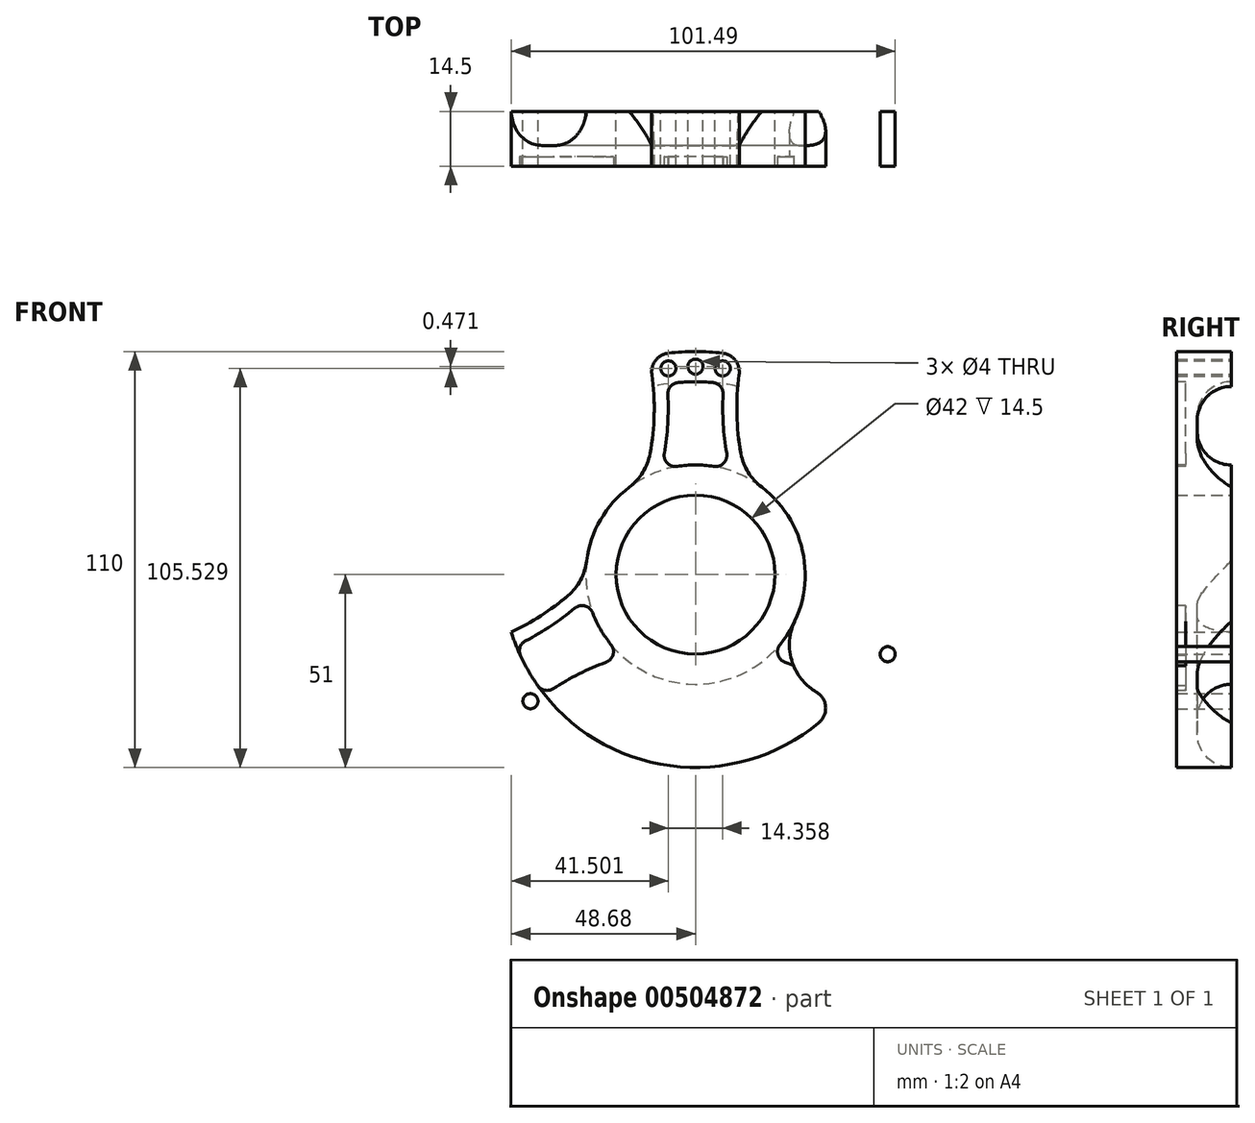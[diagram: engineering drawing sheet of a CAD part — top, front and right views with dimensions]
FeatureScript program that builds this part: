
annotation { "Feature Type Name" : "Feature", "Feature Type Description" : "" }
export const myFeature = defineFeature(function(context is Context, id is Id, definition is map)
    precondition{}
    {
        {
            var Q0;
            Q0=qCreatedBy(makeId("Front.planeOp"),FACE);
            var sketch = newSketch(context, id + "F0", { "sketchPlane" : qUnion([Q0])});
            skCircle(sketch, "E0", {"center": v(0, 0) * mm, "radius": 59 * mm});
            skCircle(sketch, "E1", {"center": v(0, 0) * mm, "radius": 51 * mm});
            skCircle(sketch, "E2", {"center": v(0, 55) * mm, "radius": 2 * mm});
            skCircle(sketch, "E3", {"center": v(7.18, 54.53) * mm, "radius": 2 * mm});
            skLineSegment(sketch, "E4", {"start": v(0, 55) * mm, "end": v(0, 0) * mm});
            skLineSegment(sketch, "E5", {"start": v(7.18, 54.53) * mm, "end": v(0, 0) * mm});
            skCircle(sketch, "E6.MirrorC", {"center": v(-7.18, 54.53) * mm, "radius": 2 * mm});
            skCircle(sketch, "E7.1.0", {"center": v(-43.63, -33.48) * mm, "radius": 2 * mm});
            skCircle(sketch, "E7.1.1", {"center": v(-47.63, -27.5) * mm, "radius": 2 * mm});
            skCircle(sketch, "E7.1.2", {"center": v(-50.81, -21.05) * mm, "radius": 2 * mm});
            skCircle(sketch, "E7.2.0", {"center": v(50.81, -21.05) * mm, "radius": 2 * mm});
            skCircle(sketch, "E7.2.1", {"center": v(47.63, -27.5) * mm, "radius": 2 * mm});
            skCircle(sketch, "E7.2.2", {"center": v(43.63, -33.48) * mm, "radius": 2 * mm});
            skCircle(sketch, "E8", {"center": v(0, 0) * mm, "radius": 21 * mm});
            skArc(sketch, "E9", {"start": v(43.78, -39.56) * mm, "mid": v(0, -22.7) * mm, "end": v(-43.78, -39.56) * mm});
            skLineSegment(sketch, "E10", {"start": v(0, -88) * mm, "end": v(43.78, -39.56) * mm});
            skLineSegment(sketch, "E11", {"start": v(0, -88) * mm, "end": v(-43.78, -39.56) * mm});
            skArc(sketch, "E12.1.0", {"start": v(12.37, 57.69) * mm, "mid": v(19.67, 11.35) * mm, "end": v(56.14, -18.13) * mm});
            skArc(sketch, "E12.2.0", {"start": v(-56.14, -18.13) * mm, "mid": v(-19.67, 11.35) * mm, "end": v(-12.37, 57.69) * mm});
            skCircle(sketch, "E13", {"center": v(0, 0) * mm, "radius": 29 * mm});
            skSolve(sketch);
        }
        {
            var Q0;
            Q0=qCreatedBy(makeId("Right.planeOp"),FACE);
            var sketch = newSketch(context, id + "F1", { "sketchPlane" : qUnion([Q0])});
            skSolve(sketch);
        }
        {
            var Q0;
            Q0=qSketchRegion(id+"F1",true);
            var Q1;
            Q1=makeQuery(id+"F0.imprint","IMPRINT",FACE,{"disambiguationData":[TD([[makeQuery(id+"F0.imprint","IMPRINT",EDGE,{"derivedFrom":sQuery(id+"F0.wireOp",EDGE,"E2")}),-1.0]])]});
            var Q2;
            {var subQ0=sQuery(id+"F0.wireOp",EDGE,"E4");var subQ1=sQuery(id+"F0.wireOp",EDGE,"E1");var subQ2=makeQuery(id+"F0.imprint","INTERSECT",VERTEX,{"derivedFrom":[subQ1,subQ0]});Q2=makeQuery(id+"F0.imprint","IMPRINT",FACE,{"disambiguationData":[TD([[makeQuery(id+"F0.imprint","IMPRINT",EDGE,{"disambiguationData":[TD([[subQ2,-1.0]])],"derivedFrom":subQ1}),1.0]])]});}
            var Q3;
            {var subQ0=sQuery(id+"F0.wireOp",EDGE,"E5");var subQ1=sQuery(id+"F0.wireOp",EDGE,"E1");var subQ2=makeQuery(id+"F0.imprint","INTERSECT",VERTEX,{"derivedFrom":[subQ1,subQ0]});Q3=makeQuery(id+"F0.imprint","IMPRINT",FACE,{"disambiguationData":[TD([[makeQuery(id+"F0.imprint","IMPRINT",EDGE,{"disambiguationData":[TD([[subQ2,-1.0]])],"derivedFrom":subQ1}),1.0]])]});}
            var Q4;
            {var subQ0=sQuery(id+"F0.wireOp",EDGE,"E5");var subQ1=sQuery(id+"F0.wireOp",EDGE,"E1");var subQ2=makeQuery(id+"F0.imprint","INTERSECT",VERTEX,{"derivedFrom":[subQ1,subQ0]});Q4=makeQuery(id+"F0.imprint","IMPRINT",FACE,{"disambiguationData":[TD([[makeQuery(id+"F0.imprint","IMPRINT",EDGE,{"disambiguationData":[TD([[subQ2,1.0]])],"derivedFrom":subQ1}),1.0]])]});}
            var Q5;
            {var subQ0=sQuery(id+"F0.wireOp",EDGE,"E13");var subQ5=sQuery(id+"F0.wireOp",EDGE,"E4");var subQ12=makeQuery(id+"F0.imprint","INTERSECT",VERTEX,{"derivedFrom":[subQ5,subQ0]});Q5=makeQuery(id+"F0.imprint","IMPRINT",FACE,{"disambiguationData":[TD([[makeQuery(id+"F0.imprint","IMPRINT",EDGE,{"disambiguationData":[TD([[subQ12,-1.0]])],"derivedFrom":subQ5}),-1.0]])]});}
            var Q6;
            {var subQ0=sQuery(id+"F0.wireOp",EDGE,"E13");var subQ1=sQuery(id+"F0.wireOp",EDGE,"E4");var subQ2=makeQuery(id+"F0.imprint","INTERSECT",VERTEX,{"derivedFrom":[subQ1,subQ0]});Q6=makeQuery(id+"F0.imprint","IMPRINT",FACE,{"disambiguationData":[TD([[makeQuery(id+"F0.imprint","IMPRINT",EDGE,{"disambiguationData":[TD([[subQ2,-1.0]])],"derivedFrom":subQ1}),1.0]])]});}
            var Q7;
            {var subQ0=sQuery(id+"F0.wireOp",EDGE,"E13");var subQ1=sQuery(id+"F0.wireOp",EDGE,"E12.2.0");var subQ2=makeQuery(id+"F0.imprint","INTERSECT",VERTEX,{"disambiguationData":[OD(0.0)],"derivedFrom":[subQ1,subQ0]});Q7=makeQuery(id+"F0.imprint","IMPRINT",FACE,{"disambiguationData":[TD([[makeQuery(id+"F0.imprint","IMPRINT",EDGE,{"disambiguationData":[TD([[subQ2,-1.0]])],"derivedFrom":subQ1}),1.0]])]});}
            var Q8;
            {var subQ0=sQuery(id+"F0.wireOp",EDGE,"E13");var subQ1=sQuery(id+"F0.wireOp",EDGE,"E12.1.0");var subQ2=makeQuery(id+"F0.imprint","INTERSECT",VERTEX,{"disambiguationData":[OD(0.0)],"derivedFrom":[subQ1,subQ0]});Q8=makeQuery(id+"F0.imprint","IMPRINT",FACE,{"disambiguationData":[TD([[makeQuery(id+"F0.imprint","IMPRINT",EDGE,{"disambiguationData":[TD([[subQ2,-1.0]])],"derivedFrom":subQ1}),1.0]])]});}
            var Q9;
            {var subQ0=sQuery(id+"F0.wireOp",EDGE,"E13");var subQ1=sQuery(id+"F0.wireOp",EDGE,"E9");var subQ2=makeQuery(id+"F0.imprint","INTERSECT",VERTEX,{"disambiguationData":[OD(0.0)],"derivedFrom":[subQ1,subQ0]});Q9=makeQuery(id+"F0.imprint","IMPRINT",FACE,{"disambiguationData":[TD([[makeQuery(id+"F0.imprint","IMPRINT",EDGE,{"disambiguationData":[TD([[subQ2,-1.0]])],"derivedFrom":subQ1}),1.0]])]});}
            var Q10;
            {var subQ0=sQuery(id+"F0.wireOp",EDGE,"E12.2.0");var subQ1=sQuery(id+"F0.wireOp",EDGE,"E1");var subQ2=makeQuery(id+"F0.imprint","INTERSECT",VERTEX,{"disambiguationData":[OD(1.0)],"derivedFrom":[subQ1,subQ0]});Q10=makeQuery(id+"F0.imprint","IMPRINT",FACE,{"disambiguationData":[TD([[makeQuery(id+"F0.imprint","IMPRINT",EDGE,{"disambiguationData":[TD([[subQ2,-1.0]])],"derivedFrom":subQ1}),1.0]])]});}
            var Q11;
            {var subQ0=sQuery(id+"F0.wireOp",EDGE,"E9");var subQ1=sQuery(id+"F0.wireOp",EDGE,"E1");var subQ2=makeQuery(id+"F0.imprint","INTERSECT",VERTEX,{"disambiguationData":[OD(1.0)],"derivedFrom":[subQ1,subQ0]});Q11=makeQuery(id+"F0.imprint","IMPRINT",FACE,{"disambiguationData":[TD([[makeQuery(id+"F0.imprint","IMPRINT",EDGE,{"disambiguationData":[TD([[subQ2,-1.0]])],"derivedFrom":subQ1}),1.0]])]});}
            var Q12;
            Q12=makeQuery(id+"F0.imprint","IMPRINT",FACE,{"disambiguationData":[TD([[makeQuery(id+"F0.imprint","IMPRINT",EDGE,{"derivedFrom":sQuery(id+"F0.wireOp",EDGE,"E7.2.0")}),1.0]])]});
            var Q13;
            Q13=makeQuery(id+"F0.imprint","IMPRINT",FACE,{"disambiguationData":[TD([[makeQuery(id+"F0.imprint","IMPRINT",EDGE,{"derivedFrom":sQuery(id+"F0.wireOp",EDGE,"E7.1.0")}),1.0]])]});
            extrude(context, id + "F2", {"entities" : qUnion([Q0, Q1, Q2, Q3, Q4, Q5, Q6, Q7, Q8, Q9, Q10, Q11, Q12, Q13]), "depth" : 14.5 * mm});
        }
        {
            var Q0;
            Q0=qCreatedBy(makeId("Right.planeOp"),FACE);
            var sketch = newSketch(context, id + "F3", { "sketchPlane" : qUnion([Q0])});
            skLineSegment(sketch, "E14.bottom", {"start": v(0, 51) * mm, "end": v(0, 51) * mm});
            skLineSegment(sketch, "E14.top", {"start": v(0, 0) * mm, "end": v(0, 0) * mm});
            skLineSegment(sketch, "E14.left", {"start": v(0, 51) * mm, "end": v(0, 29) * mm});
            skLineSegment(sketch, "E14.right", {"start": v(-9, 42) * mm, "end": v(-9, 38) * mm});
            skArc(sketch, "E15.filletArc", {"start": v(0, 51) * mm, "mid": v(-6.36, 48.36) * mm, "end": v(-9, 42) * mm});
            skArc(sketch, "E16", {"start": v(-9, 38) * mm, "mid": v(-6.36, 31.64) * mm, "end": v(0, 29) * mm});
            skSolve(sketch);
        }
        {
            var Q0;
            Q0=qSketchRegion(id+"F3",true);
            var Q1;
            Q1=sQuery(id+"F0.wireOp",EDGE,"E0");
            revolve(context, id + "F4", {"operationType" : NewBodyOperationType.REMOVE, "entities" : qUnion([Q0]), "axis" : qUnion([Q1]), "revolveType" : RevolveType.FULL});
        }
        {
            var Q0;
            {var subQ0=sQuery(id+"F0.wireOp",EDGE,"E13");var subQ1=sQuery(id+"F0.wireOp",EDGE,"E12.1.0");Q0=makeQuery(id+"F2.opExtrude","SWEPT_EDGE",EDGE,{"disambiguationData":[OSD([subQ1,subQ0]),TDD([makeQuery(id+"F0.imprint","INTERSECT",VERTEX,{"disambiguationData":[OD(0.0)],"derivedFrom":[subQ1,subQ0]})])]});}
            var Q1;
            {var subQ0=sQuery(id+"F0.wireOp",EDGE,"E13");var subQ1=sQuery(id+"F0.wireOp",EDGE,"E12.1.0");Q1=makeQuery(id+"F2.opExtrude","SWEPT_EDGE",EDGE,{"disambiguationData":[OSD([subQ1,subQ0]),TDD([makeQuery(id+"F0.imprint","INTERSECT",VERTEX,{"disambiguationData":[OD(1.0)],"derivedFrom":[subQ1,subQ0]})])]});}
            var Q2;
            {var subQ0=sQuery(id+"F0.wireOp",EDGE,"E13");var subQ1=sQuery(id+"F0.wireOp",EDGE,"E12.2.0");Q2=makeQuery(id+"F2.opExtrude","SWEPT_EDGE",EDGE,{"disambiguationData":[OSD([subQ1,subQ0]),TDD([makeQuery(id+"F0.imprint","INTERSECT",VERTEX,{"disambiguationData":[OD(0.0)],"derivedFrom":[subQ1,subQ0]})])]});}
            var Q3;
            {var subQ0=sQuery(id+"F0.wireOp",EDGE,"E13");var subQ1=sQuery(id+"F0.wireOp",EDGE,"E12.2.0");Q3=makeQuery(id+"F2.opExtrude","SWEPT_EDGE",EDGE,{"disambiguationData":[OSD([subQ1,subQ0]),TDD([makeQuery(id+"F0.imprint","INTERSECT",VERTEX,{"disambiguationData":[OD(1.0)],"derivedFrom":[subQ1,subQ0]})])]});}
            var Q4;
            {var subQ0=sQuery(id+"F0.wireOp",EDGE,"E13");var subQ1=sQuery(id+"F0.wireOp",EDGE,"E9");Q4=makeQuery(id+"F2.opExtrude","SWEPT_EDGE",EDGE,{"disambiguationData":[OSD([subQ1,subQ0]),TDD([makeQuery(id+"F0.imprint","INTERSECT",VERTEX,{"disambiguationData":[OD(1.0)],"derivedFrom":[subQ1,subQ0]})])]});}
            var Q5;
            {var subQ0=sQuery(id+"F0.wireOp",EDGE,"E13");var subQ1=sQuery(id+"F0.wireOp",EDGE,"E9");Q5=makeQuery(id+"F2.opExtrude","SWEPT_EDGE",EDGE,{"disambiguationData":[OSD([subQ1,subQ0]),TDD([makeQuery(id+"F0.imprint","INTERSECT",VERTEX,{"disambiguationData":[OD(0.0)],"derivedFrom":[subQ1,subQ0]})])]});}
            fillet(context, id + "F5", {"entities" : qUnion([Q0, Q1, Q2, Q3, Q4, Q5]), "radius" : 14.5 * mm, "tangentPropagation" : true, "allowEdgeOverflow" : false});
        }
        {
            var Q0;
            {var subQ0=sQuery(id+"F0.wireOp",EDGE,"E12.1.0");var subQ1=sQuery(id+"F0.wireOp",EDGE,"E0");Q0=makeQuery(id+"F2.opExtrude","SWEPT_EDGE",EDGE,{"disambiguationData":[OSD([subQ1,subQ0]),TDD([makeQuery(id+"F0.imprint","INTERSECT",VERTEX,{"disambiguationData":[OD(0.0)],"derivedFrom":[subQ1,subQ0]})])]});}
            var Q1;
            {var subQ0=sQuery(id+"F0.wireOp",EDGE,"E12.2.0");var subQ1=sQuery(id+"F0.wireOp",EDGE,"E0");Q1=makeQuery(id+"F2.opExtrude","SWEPT_EDGE",EDGE,{"disambiguationData":[OSD([subQ1,subQ0]),TDD([makeQuery(id+"F0.imprint","INTERSECT",VERTEX,{"disambiguationData":[OD(1.0)],"derivedFrom":[subQ1,subQ0]})])]});}
            var Q2;
            {var subQ0=sQuery(id+"F0.wireOp",EDGE,"E12.2.0");var subQ1=sQuery(id+"F0.wireOp",EDGE,"E0");Q2=makeQuery(id+"F2.opExtrude","SWEPT_EDGE",EDGE,{"disambiguationData":[OSD([subQ1,subQ0]),TDD([makeQuery(id+"F0.imprint","INTERSECT",VERTEX,{"disambiguationData":[OD(0.0)],"derivedFrom":[subQ1,subQ0]})])]});}
            var Q3;
            {var subQ0=sQuery(id+"F0.wireOp",EDGE,"E12.1.0");var subQ1=sQuery(id+"F0.wireOp",EDGE,"E0");Q3=makeQuery(id+"F2.opExtrude","SWEPT_EDGE",EDGE,{"disambiguationData":[OSD([subQ1,subQ0]),TDD([makeQuery(id+"F0.imprint","INTERSECT",VERTEX,{"disambiguationData":[OD(1.0)],"derivedFrom":[subQ1,subQ0]})])]});}
            var Q4;
            Q4=makeQuery(id+"F2.opExtrude","SWEPT_EDGE",EDGE,{"disambiguationData":[OSD([sQuery(id+"F0.wireOp",EDGE,"E0"),sQuery(id+"F0.wireOp",EDGE,"E9"),sQuery(id+"F0.wireOp",EDGE,"E11")])]});
            var Q5;
            Q5=makeQuery(id+"F2.opExtrude","SWEPT_EDGE",EDGE,{"disambiguationData":[OSD([sQuery(id+"F0.wireOp",EDGE,"E0"),sQuery(id+"F0.wireOp",EDGE,"E9"),sQuery(id+"F0.wireOp",EDGE,"E10")])]});
            fillet(context, id + "F6", {"entities" : qUnion([Q0, Q1, Q2, Q3, Q4, Q5]), "radius" : 5 * mm, "tangentPropagation" : true, "allowEdgeOverflow" : false});
        }
        {
            var Q0;
            Q0=makeQuery(id+"F2.opExtrude","CAP_FACE",FACE,{"disambiguationData":[OSD([sQuery(id+"F0.wireOp",EDGE,"E0"),sQuery(id+"F0.wireOp",EDGE,"E2"),sQuery(id+"F0.wireOp",EDGE,"E3"),sQuery(id+"F0.wireOp",EDGE,"E6.MirrorC"),sQuery(id+"F0.wireOp",EDGE,"E7.1.0"),sQuery(id+"F0.wireOp",EDGE,"E7.1.1"),sQuery(id+"F0.wireOp",EDGE,"E7.1.2"),sQuery(id+"F0.wireOp",EDGE,"E7.2.0"),sQuery(id+"F0.wireOp",EDGE,"E7.2.1"),sQuery(id+"F0.wireOp",EDGE,"E7.2.2"),sQuery(id+"F0.wireOp",EDGE,"E8"),sQuery(id+"F0.wireOp",EDGE,"E9"),sQuery(id+"F0.wireOp",EDGE,"E12.1.0"),sQuery(id+"F0.wireOp",EDGE,"E12.2.0"),sQuery(id+"F0.wireOp",EDGE,"E13")])],"isStart":false});
            var sketch = newSketch(context, id + "F7", { "sketchPlane" : qUnion([Q0])});
            skArc(sketch, "E17", {"start": v(22.37, -18.45) * mm, "mid": v(25.11, -14.5) * mm, "end": v(27.17, -10.15) * mm});
            skArc(sketch, "E18", {"start": v(-46.28, -21.43) * mm, "mid": v(-44.17, -25.5) * mm, "end": v(-41.7, -29.36) * mm});
            skArc(sketch, "E19", {"start": v(-44.92, -17.5) * mm, "mid": v(-38.17, -13.56) * mm, "end": v(-31.9, -8.9) * mm});
            skArc(sketch, "E20", {"start": v(7.3, 47.65) * mm, "mid": v(7.34, 39.84) * mm, "end": v(8.25, 32.08) * mm});
            skArc(sketch, "E21.trimOffspring", {"start": v(-8.25, 32.08) * mm, "mid": v(-7.34, 39.84) * mm, "end": v(-7.3, 47.65) * mm});
            skArc(sketch, "E22.trimOffspring", {"start": v(31.9, -8.9) * mm, "mid": v(38.17, -13.56) * mm, "end": v(44.92, -17.5) * mm});
            skArc(sketch, "E23", {"start": v(37.61, -30.15) * mm, "mid": v(30.83, -26.27) * mm, "end": v(23.66, -23.18) * mm});
            skArc(sketch, "E24.trimOffspring", {"start": v(-23.66, -23.18) * mm, "mid": v(-30.83, -26.27) * mm, "end": v(-37.61, -30.15) * mm});
            skArc(sketch, "E25.trimOffspring", {"start": v(4.58, 50.8) * mm, "mid": v(0, 51) * mm, "end": v(-4.58, 50.8) * mm});
            skArc(sketch, "E26.trimOffspring", {"start": v(41.7, -29.36) * mm, "mid": v(44.17, -25.5) * mm, "end": v(46.28, -21.43) * mm});
            skArc(sketch, "E27.trimOffspring", {"start": v(4.8, 28.6) * mm, "mid": v(0, 29) * mm, "end": v(-4.8, 28.6) * mm});
            skArc(sketch, "E28.trimOffspring", {"start": v(-27.17, -10.15) * mm, "mid": v(-25.11, -14.5) * mm, "end": v(-22.37, -18.45) * mm});
            skPoint(sketch, "E29.visualSharp", {"position": v(-9.21, 27.5) * mm});
            skArc(sketch, "E29.filletArc", {"start": v(-8.25, 32.08) * mm, "mid": v(-7.42, 29.45) * mm, "end": v(-4.8, 28.6) * mm});
            skPoint(sketch, "E30.visualSharp", {"position": v(9.21, 27.5) * mm});
            skArc(sketch, "E30.filletArc", {"start": v(4.8, 28.6) * mm, "mid": v(7.42, 29.45) * mm, "end": v(8.25, 32.08) * mm});
            skPoint(sketch, "E31.visualSharp", {"position": v(-7.51, 50.44) * mm});
            skArc(sketch, "E31.filletArc", {"start": v(-4.58, 50.8) * mm, "mid": v(-6.58, 49.77) * mm, "end": v(-7.3, 47.65) * mm});
            skPoint(sketch, "E32.visualSharp", {"position": v(7.51, 50.44) * mm});
            skArc(sketch, "E32.filletArc", {"start": v(7.3, 47.65) * mm, "mid": v(6.58, 49.77) * mm, "end": v(4.58, 50.8) * mm});
            skPoint(sketch, "E33.visualSharp", {"position": v(-28.42, -5.77) * mm});
            skArc(sketch, "E33.filletArc", {"start": v(-27.17, -10.15) * mm, "mid": v(-29.21, -8.3) * mm, "end": v(-31.9, -8.9) * mm});
            skPoint(sketch, "E34.visualSharp", {"position": v(-19.2, -21.73) * mm});
            skArc(sketch, "E34.filletArc", {"start": v(-23.66, -23.18) * mm, "mid": v(-21.79, -21.15) * mm, "end": v(-22.37, -18.45) * mm});
            skPoint(sketch, "E35.visualSharp", {"position": v(-39.93, -31.73) * mm});
            skArc(sketch, "E35.filletArc", {"start": v(-41.7, -29.36) * mm, "mid": v(-39.81, -30.58) * mm, "end": v(-37.61, -30.15) * mm});
            skPoint(sketch, "E36.visualSharp", {"position": v(-47.44, -18.72) * mm});
            skArc(sketch, "E36.filletArc", {"start": v(-44.92, -17.5) * mm, "mid": v(-46.4, -19.19) * mm, "end": v(-46.28, -21.43) * mm});
            skPoint(sketch, "E37.visualSharp", {"position": v(28.42, -5.77) * mm});
            skArc(sketch, "E37.filletArc", {"start": v(31.9, -8.9) * mm, "mid": v(29.21, -8.3) * mm, "end": v(27.17, -10.15) * mm});
            skPoint(sketch, "E38.visualSharp", {"position": v(47.44, -18.72) * mm});
            skArc(sketch, "E38.filletArc", {"start": v(46.28, -21.43) * mm, "mid": v(46.4, -19.19) * mm, "end": v(44.92, -17.5) * mm});
            skPoint(sketch, "E39.visualSharp", {"position": v(39.93, -31.73) * mm});
            skArc(sketch, "E39.filletArc", {"start": v(37.61, -30.15) * mm, "mid": v(39.81, -30.58) * mm, "end": v(41.7, -29.36) * mm});
            skPoint(sketch, "E40.visualSharp", {"position": v(19.2, -21.73) * mm});
            skArc(sketch, "E40.filletArc", {"start": v(22.37, -18.45) * mm, "mid": v(21.79, -21.15) * mm, "end": v(23.66, -23.18) * mm});
            skSolve(sketch);
        }
        {
            var Q0;
            Q0 = qSketchRegion(id + "F7", true);
            extrude(context, id + "F8", {"entities" : qUnion([Q0]), "operationType" : NewBodyOperationType.REMOVE, "oppositeDirection" : true, "depth" : 2.5 * mm});
        }
    });
